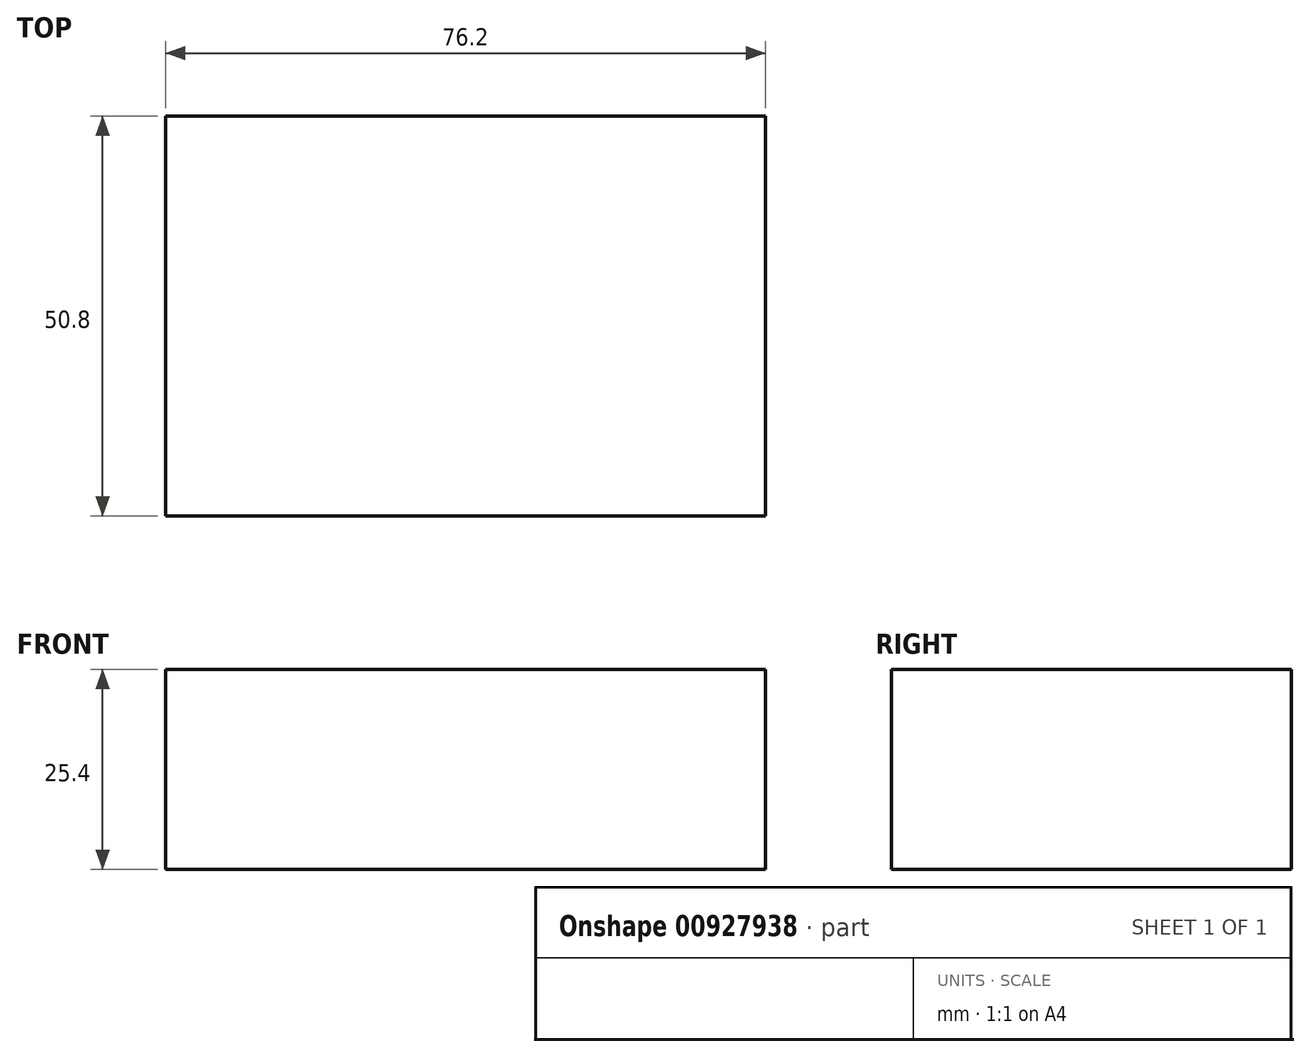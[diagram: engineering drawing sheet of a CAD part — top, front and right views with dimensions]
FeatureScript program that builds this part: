
annotation { "Feature Type Name" : "Feature", "Feature Type Description" : "" }
export const myFeature = defineFeature(function(context is Context, id is Id, definition is map)
    precondition{}
    {
        {
            var Q0;
            Q0=qCreatedBy(makeId("Front.planeOp"),FACE);
            var sketch = newSketch(context, id + "F0", { "sketchPlane" : qUnion([Q0])});
            skLineSegment(sketch, "E0.bottom", {"start": v(-26.97, 8.81) * mm, "end": v(49.23, 8.81) * mm});
            skLineSegment(sketch, "E0.top", {"start": v(-26.97, -16.59) * mm, "end": v(49.23, -16.59) * mm});
            skLineSegment(sketch, "E0.left", {"start": v(-26.97, 8.81) * mm, "end": v(-26.97, -16.59) * mm});
            skLineSegment(sketch, "E0.right", {"start": v(49.23, 8.81) * mm, "end": v(49.23, -16.59) * mm});
            skLineSegment(sketch, "E1", {"start": v(11.13, 63.37) * mm, "end": v(11.13, 8.81) * mm});
            skPoint(sketch, "E1.endSnap0", {"position": v(11.13, 8.81) * mm});
            skSolve(sketch);
        }
        {
            var Q0;
            Q0=makeQuery(id+"F0.imprint","IMPRINT",FACE,{"disambiguationData":[TD([[makeQuery(id+"F0.imprint","IMPRINT",EDGE,{"derivedFrom":sQuery(id+"F0.wireOp",EDGE,"E0.bottom")}),-1.0]])]});
            extrude(context, id + "F1", {"entities" : qUnion([Q0]), "depth" : 50.8 * mm, "offsetDistance" : 25.4 * mm});
        }
    });
